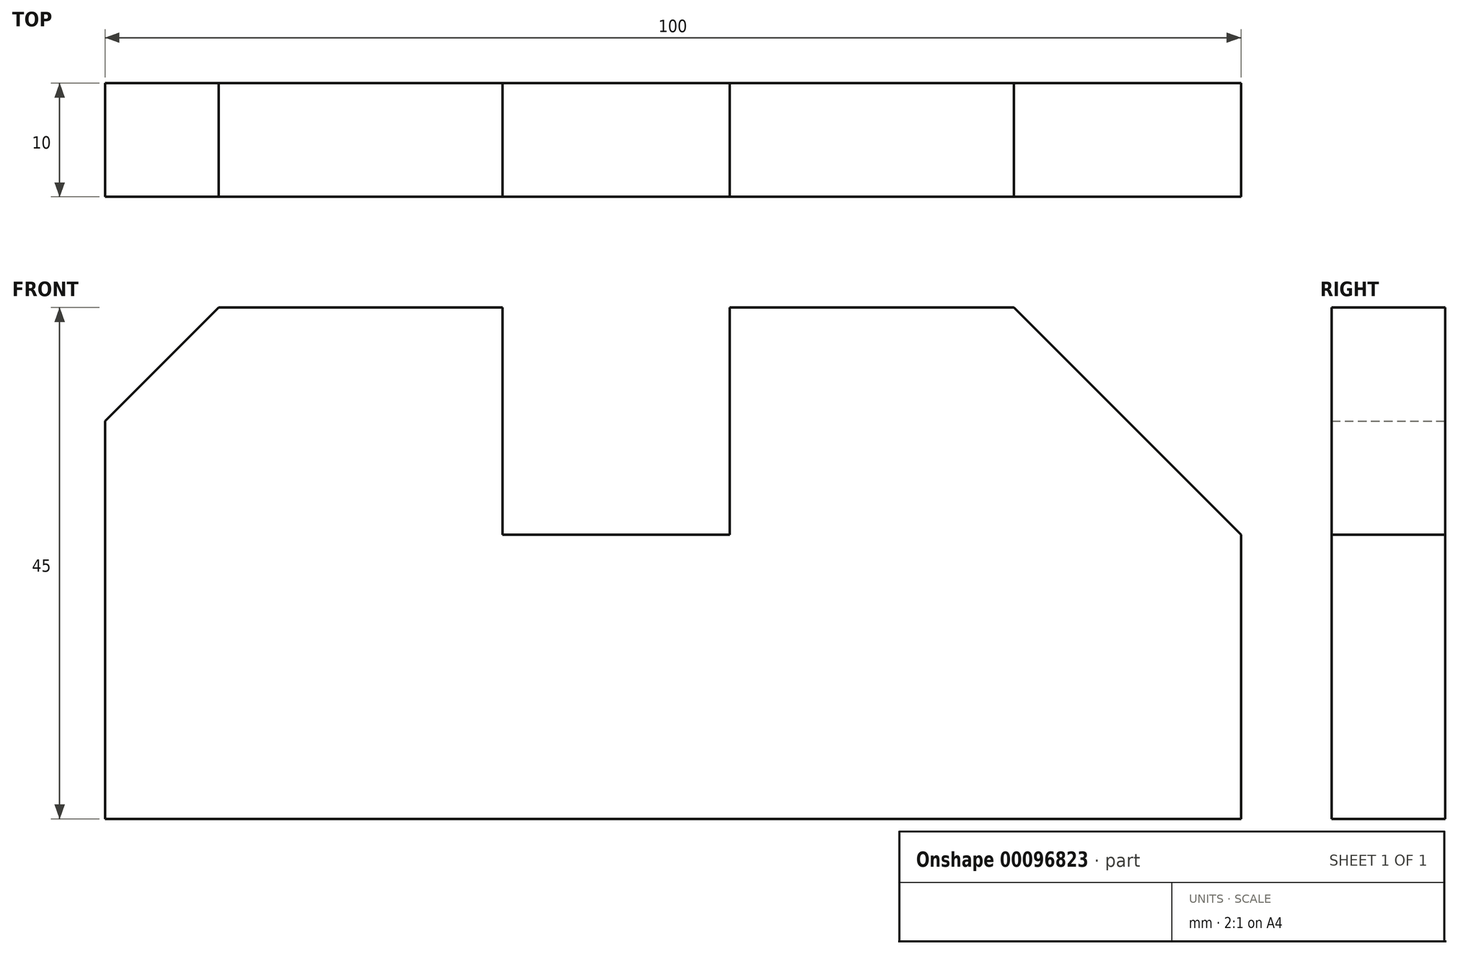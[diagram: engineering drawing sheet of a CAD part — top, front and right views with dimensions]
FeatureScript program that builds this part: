
annotation { "Feature Type Name" : "Feature", "Feature Type Description" : "" }
export const myFeature = defineFeature(function(context is Context, id is Id, definition is map)
    precondition{}
    {
        {
            var Q0;
            Q0=qCreatedBy(makeId("Front.planeOp"),FACE);
            var sketch = newSketch(context, id + "F0", { "sketchPlane" : qUnion([Q0])});
            skLineSegment(sketch, "E0", {"start": v(0, 0) * mm, "end": v(100, 0) * mm});
            skLineSegment(sketch, "E1", {"start": v(100, 0) * mm, "end": v(100, 25) * mm});
            skLineSegment(sketch, "E2", {"start": v(100, 25) * mm, "end": v(80, 45) * mm});
            skLineSegment(sketch, "E3", {"start": v(80, 45) * mm, "end": v(55, 45) * mm});
            skLineSegment(sketch, "E4", {"start": v(55, 45) * mm, "end": v(55, 25) * mm});
            skLineSegment(sketch, "E5", {"start": v(55, 25) * mm, "end": v(35, 25) * mm});
            skLineSegment(sketch, "E6", {"start": v(35, 25) * mm, "end": v(35, 45) * mm});
            skLineSegment(sketch, "E7", {"start": v(35, 45) * mm, "end": v(10, 45) * mm});
            skLineSegment(sketch, "E8", {"start": v(10, 45) * mm, "end": v(0, 35) * mm});
            skLineSegment(sketch, "E9", {"start": v(0, 35) * mm, "end": v(0, 0) * mm});
            skSolve(sketch);
        }
        {
            var Q0;
            Q0 = qSketchRegion(id + "F0", true);
            extrude(context, id + "F1", {"entities" : qUnion([Q0]), "depth" : 10 * mm});
        }
    });
